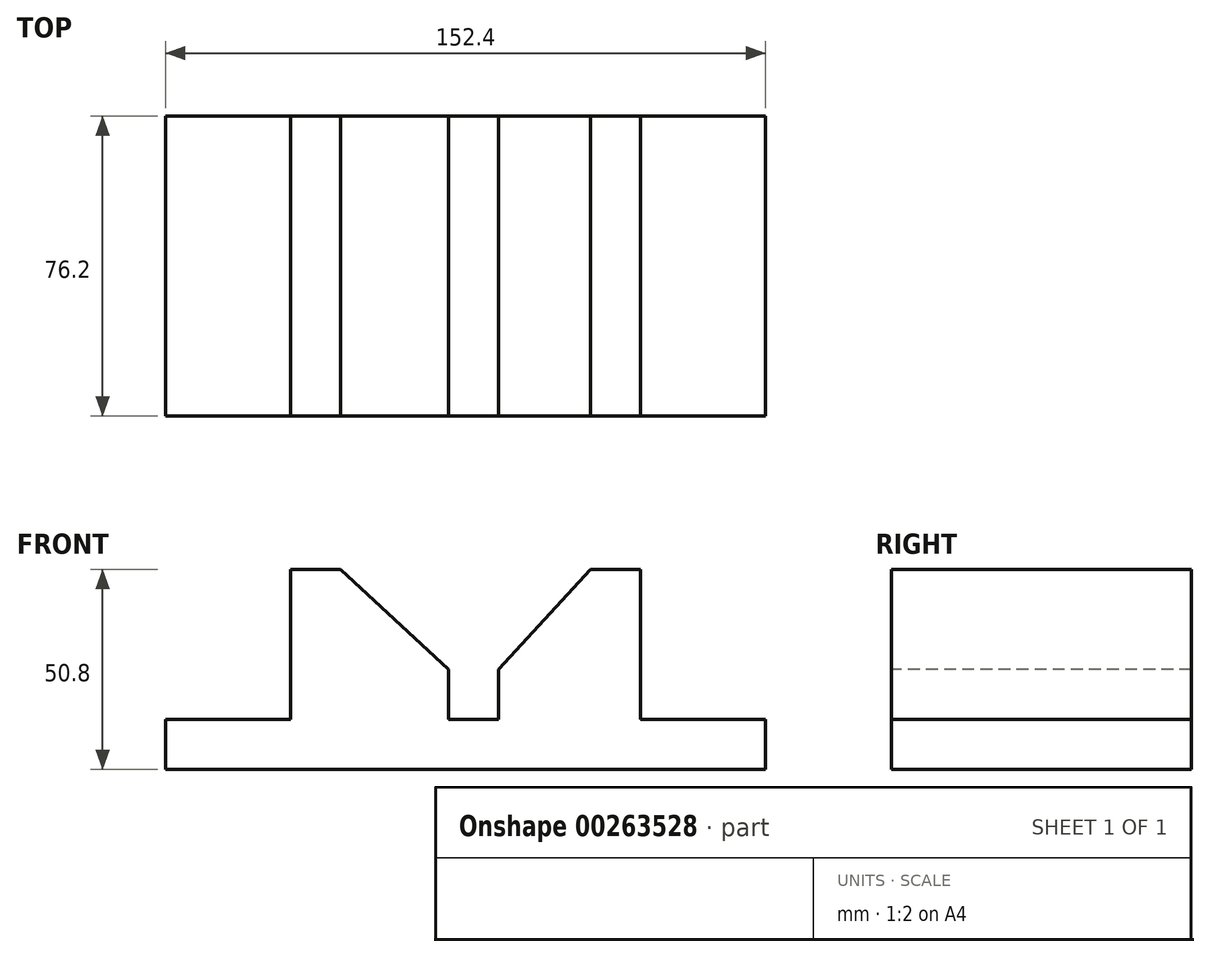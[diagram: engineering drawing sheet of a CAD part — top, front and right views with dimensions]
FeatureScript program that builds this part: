
annotation { "Feature Type Name" : "Feature", "Feature Type Description" : "" }
export const myFeature = defineFeature(function(context is Context, id is Id, definition is map)
    precondition{}
    {
        {
            var Q0;
            Q0=qCreatedBy(makeId("Front.planeOp"),FACE);
            var sketch = newSketch(context, id + "F0", { "sketchPlane" : qUnion([Q0])});
            skLineSegment(sketch, "E0", {"start": v(-71.88, 0) * mm, "end": v(80.52, 0) * mm});
            skLineSegment(sketch, "E1", {"start": v(80.52, 0) * mm, "end": v(80.52, 12.7) * mm});
            skLineSegment(sketch, "E2", {"start": v(80.52, 12.7) * mm, "end": v(48.77, 12.7) * mm});
            skLineSegment(sketch, "E3", {"start": v(48.77, 12.7) * mm, "end": v(48.77, 50.8) * mm});
            skLineSegment(sketch, "E4", {"start": v(-71.88, 0) * mm, "end": v(-71.88, 12.7) * mm});
            skLineSegment(sketch, "E5", {"start": v(-71.88, 12.7) * mm, "end": v(-40.13, 12.7) * mm});
            skLineSegment(sketch, "E6", {"start": v(-40.13, 12.7) * mm, "end": v(-40.13, 50.8) * mm});
            skLineSegment(sketch, "E7", {"start": v(-40.13, 50.8) * mm, "end": v(-27.43, 50.8) * mm});
            skLineSegment(sketch, "E8", {"start": v(48.77, 50.8) * mm, "end": v(36.07, 50.8) * mm});
            skLineSegment(sketch, "E9", {"start": v(12.7, 12.7) * mm, "end": v(12.7, 25.4) * mm});
            skLineSegment(sketch, "E10", {"start": v(12.7, 25.4) * mm, "end": v(36.07, 50.8) * mm});
            skLineSegment(sketch, "E11", {"start": v(12.7, 12.7) * mm, "end": v(0, 12.7) * mm});
            skLineSegment(sketch, "E12", {"start": v(0, 12.7) * mm, "end": v(0, 25.4) * mm});
            skLineSegment(sketch, "E13", {"start": v(0, 25.4) * mm, "end": v(-27.43, 50.8) * mm});
            skSolve(sketch);
        }
        {
            var Q0;
            Q0 = qSketchRegion(id + "F0", true);
            extrude(context, id + "F1", {"entities" : qUnion([Q0]), "oppositeDirection" : true, "depth" : 76.2 * mm});
        }
    });
